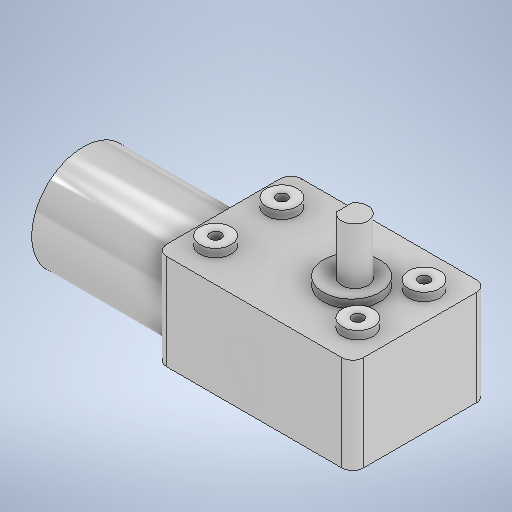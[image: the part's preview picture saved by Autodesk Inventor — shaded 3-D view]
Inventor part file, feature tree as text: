
AUTODESK INVENTOR PART (.ipt)
format: ipt  version: 2025.2 (Build 292293000, 293)  size: 330,752 bytes
history: native  units: in
note: dims shown in document units (in); Inventor stores cm internally (conversion verified against a paired STEP export)
features: extrude x10, sketch x10, fillet x1
ambient origin geometry x8: Origin, YZ Plane, XZ Plane, XY Plane, X Axis, Y Axis, Z Axis, Center Point
bodies: Solid1 (feature_tree)
feature tree (21):
  extrude  "Extrusion1"  Depth=1.81in
  extrude  "Extrusion2"  Depth=0.62in
  extrude  "Extrusion3"  Depth=0.88in
  fillet  "Fillet1"  Radius=0.7in
  extrude  "Extrusion4"  Depth=1.21in TaperAngle=0.0deg
  extrude  "Extrusion5"  Depth=0.6in
  sketch  "Sketch8"  dims[d13=0.59in d14=0.0in d15=0.1in]
  sketch  "Sketch9"  dims[d16=0.024in d17=0.59in d18=0.0in]
  sketch  "Sketch10"  dims[d22=0.285in d23=0.285in]
  extrude  "Extrusion6"  Depth=0.1in
  extrude  "Extrusion7"  Depth=0.59in TaperAngle=0.0deg
  extrude  "Extrusion8"  Depth=0.285in
  extrude  "Extrusion9"  Depth=0.285in
  extrude  "Extrusion10"  Depth=0.075in
  sketch  "Sketch1"  dims[d0=1.81in d1=1.24in]
  sketch  "Sketch2"  dims[d2=0.905in d3=0.62in]
  sketch  "Sketch3"  dims[d4=0.88in d5=0.0in d6=0.95in d7=0.7in]
  sketch  "Sketch4"  dims[d8=0.525in d9=1.21in d10=0.0in]
  sketch  "Sketch6"  dims[d11=0.24in d12=0.6in]
  sketch  "Sketch11"  dims[d24=0.285in d25=0.285in]
  sketch  "Sketch12"  dims[d26=0.3145in d27=0.315in d28=0.0in d29=0.0in d30=0.0in d31=0.2675in d32=1.31in d33=0.0in d34=0.075in d35=0.0in d36=0.1in d37=0.1in d38=0.1in d39=0.1in d40=0.1in d41=0.0in d42=0.1in d43=0.0in d44=0.1in d45=0.0in d46=0.1in d47=0.0in d48=0.52in d49=0.63in d50=0.075in d51=0.0in]
